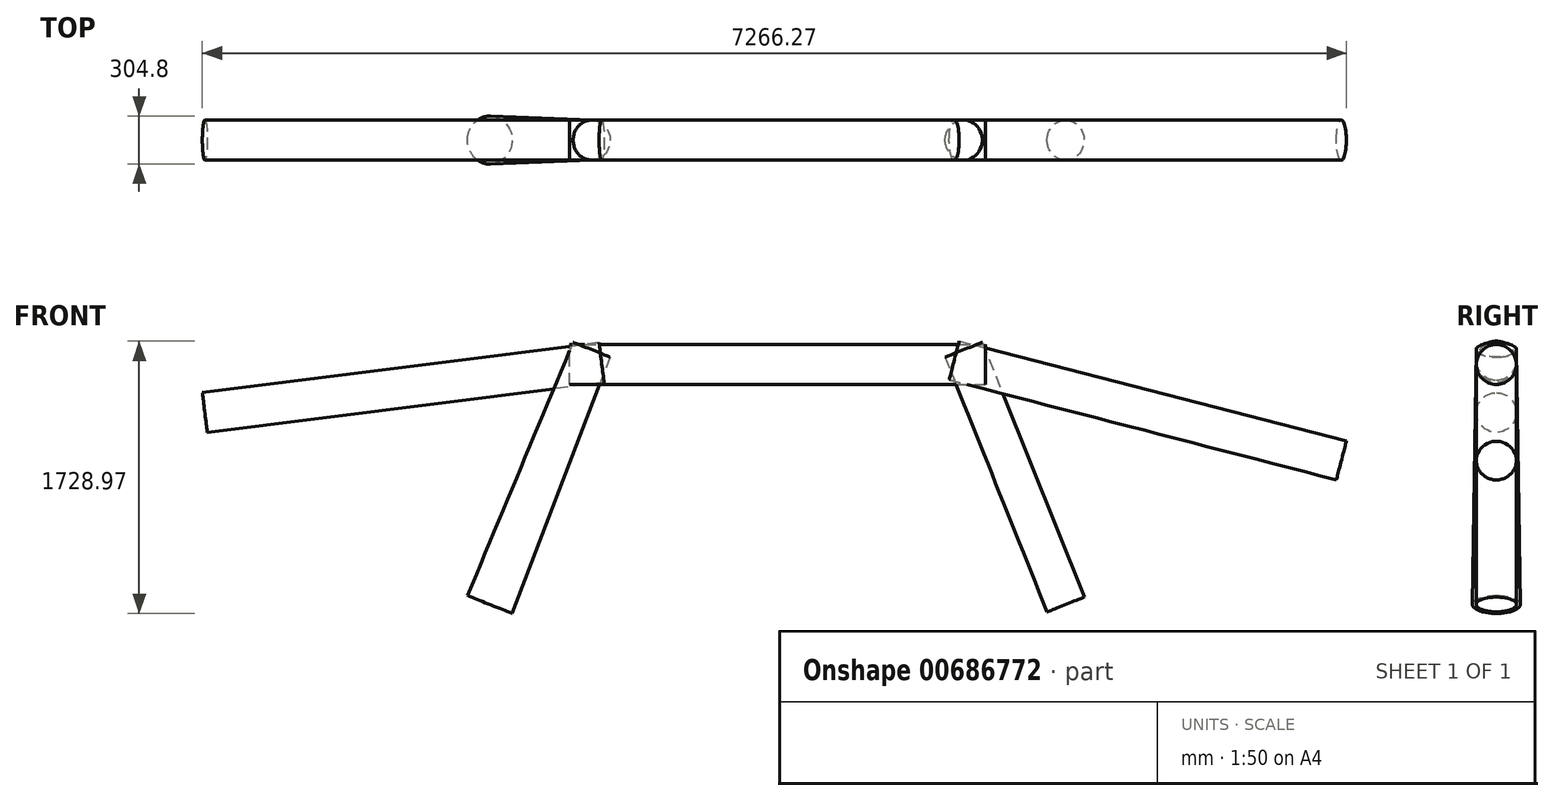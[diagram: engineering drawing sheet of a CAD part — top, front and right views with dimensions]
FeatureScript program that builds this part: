
annotation { "Feature Type Name" : "Feature", "Feature Type Description" : "" }
export const myFeature = defineFeature(function(context is Context, id is Id, definition is map)
    precondition{}
    {
        {
            var Q0;
            Q0=qCreatedBy(makeId("Front.planeOp"),FACE);
            var sketch = newSketch(context, id + "F0", { "sketchPlane" : qUnion([Q0])});
            skLineSegment(sketch, "E0", {"start": v(-1320.8, 0) * mm, "end": v(-1219.2, 0) * mm, "construction": true});
            skLineSegment(sketch, "E1", {"start": v(-1219.2, 0) * mm, "end": v(1219.2, 0) * mm, "construction": true});
            skLineSegment(sketch, "E2", {"start": v(1219.2, 0) * mm, "end": v(1320.8, 0) * mm, "construction": true});
            skLineSegment(sketch, "E3", {"start": v(-1181.47, 94.33) * mm, "end": v(-1219.2, 0) * mm, "construction": true});
            skLineSegment(sketch, "E4", {"start": v(-1219.2, 0) * mm, "end": v(-1828.8, -1524) * mm, "construction": true});
            skLineSegment(sketch, "E5", {"start": v(1181.47, 94.33) * mm, "end": v(1219.2, 0) * mm, "construction": true});
            skLineSegment(sketch, "E6", {"start": v(1219.2, 0) * mm, "end": v(1828.8, -1524) * mm, "construction": true});
            skLineSegment(sketch, "E7", {"start": v(1120.83, 25.4) * mm, "end": v(1219.2, 0) * mm, "construction": true});
            skLineSegment(sketch, "E8", {"start": v(1219.2, 0) * mm, "end": v(3580.17, -609.6) * mm, "construction": true});
            skLineSegment(sketch, "E9", {"start": v(-1118.4, 12.7) * mm, "end": v(-1219.2, 0) * mm, "construction": true});
            skLineSegment(sketch, "E10", {"start": v(-1219.2, 0) * mm, "end": v(-3638.47, -304.8) * mm, "construction": true});
            skSolve(sketch);
        }
        {
            var Q0;
            Q0=sQuery(id+"F0.wireOp",EDGE,"E10");
            var Q1;
            Q1=sQuery(id+"F0.wireOp",VERTEX,"E10.end");
            cPlane(context, id + "F1", {"entities" : qUnion([Q0, Q1]), "cplaneType" : CPlaneType.LINE_POINT, "offset" : 25.4 * mm, "width" : 152.4 * mm, "height" : 152.4 * mm});
        }
        {
            var Q0;
            Q0=sQuery(id+"F0.wireOp",VERTEX,"E9.start");
            var Q1;
            Q1=sQuery(id+"F0.wireOp",EDGE,"E9");
            cPlane(context, id + "F2", {"entities" : qUnion([Q0, Q1]), "cplaneType" : CPlaneType.LINE_POINT, "offset" : 25.4 * mm, "width" : 152.4 * mm, "height" : 152.4 * mm});
        }
        {
            var Q0;
            Q0=qCreatedBy(id+"F1.planeOp",FACE);
            var sketch = newSketch(context, id + "F3", { "sketchPlane" : qUnion([Q0])});
            skCircle(sketch, "E11", {"center": v(0, 152.4) * mm, "radius": 127 * mm});
            skSolve(sketch);
        }
        {
            var Q0;
            Q0=qCreatedBy(id+"F2.planeOp",FACE);
            var sketch = newSketch(context, id + "F4", { "sketchPlane" : qUnion([Q0])});
            skCircle(sketch, "E12", {"center": v(0, 152.4) * mm, "radius": 127 * mm});
            skSolve(sketch);
        }
        {
            var Q0;
            Q0=makeQuery(id+"F3.imprint","IMPRINT",FACE,{"disambiguationData":[TD([[makeQuery(id+"F3.imprint","IMPRINT",EDGE,{"derivedFrom":sQuery(id+"F3.wireOp",EDGE,"E11")}),1.0]])]});
            var Q1;
            Q1=makeQuery(id+"F4.imprint","IMPRINT",FACE,{"disambiguationData":[TD([[makeQuery(id+"F4.imprint","IMPRINT",EDGE,{"derivedFrom":sQuery(id+"F4.wireOp",EDGE,"E12")}),1.0]])]});
            loft(context, id + "F5", {"sheetProfilesArray" : [{ "sheetProfileEntities" : qUnion([Q0]) }, { "sheetProfileEntities" : qUnion([Q1]) }]});
        }
        {
            var Q0;
            Q0=sQuery(id+"F0.wireOp",EDGE,"E4");
            var Q1;
            Q1=sQuery(id+"F0.wireOp",VERTEX,"E4.end");
            cPlane(context, id + "F6", {"entities" : qUnion([Q0, Q1]), "cplaneType" : CPlaneType.LINE_POINT, "offset" : 25.4 * mm, "width" : 152.4 * mm, "height" : 152.4 * mm});
        }
        {
            var Q0;
            Q0=sQuery(id+"F0.wireOp",VERTEX,"E3.start");
            var Q1;
            Q1=sQuery(id+"F0.wireOp",EDGE,"E3");
            cPlane(context, id + "F7", {"entities" : qUnion([Q0, Q1]), "cplaneType" : CPlaneType.LINE_POINT, "offset" : 25.4 * mm, "width" : 152.4 * mm, "height" : 152.4 * mm});
        }
        {
            var Q0;
            Q0=qCreatedBy(id+"F6.planeOp",FACE);
            var sketch = newSketch(context, id + "F8", { "sketchPlane" : qUnion([Q0])});
            skCircle(sketch, "E13", {"center": v(-1132, 0) * mm, "radius": 152.4 * mm});
            skSolve(sketch);
        }
        {
            var Q0;
            Q0=qCreatedBy(id+"F7.planeOp",FACE);
            var sketch = newSketch(context, id + "F9", { "sketchPlane" : qUnion([Q0])});
            skCircle(sketch, "E14", {"center": v(-1132, 0) * mm, "radius": 127 * mm});
            skSolve(sketch);
        }
        {
            var Q0;
            Q0=makeQuery(id+"F8.imprint","IMPRINT",FACE,{"disambiguationData":[TD([[makeQuery(id+"F8.imprint","IMPRINT",EDGE,{"derivedFrom":sQuery(id+"F8.wireOp",EDGE,"E13")}),1.0]])]});
            var Q1;
            Q1=makeQuery(id+"F9.imprint","IMPRINT",FACE,{"disambiguationData":[TD([[makeQuery(id+"F9.imprint","IMPRINT",EDGE,{"derivedFrom":sQuery(id+"F9.wireOp",EDGE,"E14")}),1.0]])]});
            loft(context, id + "F10", {"sheetProfilesArray" : [{ "sheetProfileEntities" : qUnion([Q0]) }, { "sheetProfileEntities" : qUnion([Q1]) }]});
        }
        {
            var Q0;
            Q0=sQuery(id+"F0.wireOp",EDGE,"E0");
            var Q1;
            Q1=sQuery(id+"F0.wireOp",VERTEX,"E0.start");
            cPlane(context, id + "F11", {"entities" : qUnion([Q0, Q1]), "cplaneType" : CPlaneType.LINE_POINT, "offset" : 25.4 * mm, "width" : 152.4 * mm, "height" : 152.4 * mm});
        }
        {
            var Q0;
            Q0=sQuery(id+"F0.wireOp",EDGE,"E2");
            var Q1;
            Q1=sQuery(id+"F0.wireOp",VERTEX,"E2.end");
            cPlane(context, id + "F12", {"entities" : qUnion([Q0, Q1]), "cplaneType" : CPlaneType.LINE_POINT, "offset" : 25.4 * mm, "width" : 152.4 * mm, "height" : 152.4 * mm});
        }
        {
            var Q0;
            Q0=qCreatedBy(id+"F12.planeOp",FACE);
            var sketch = newSketch(context, id + "F13", { "sketchPlane" : qUnion([Q0])});
            skCircle(sketch, "E15", {"center": v(0, 0) * mm, "radius": 127 * mm});
            skSolve(sketch);
        }
        {
            var Q0;
            Q0=qCreatedBy(id+"F11.planeOp",FACE);
            var sketch = newSketch(context, id + "F14", { "sketchPlane" : qUnion([Q0])});
            skCircle(sketch, "E16", {"center": v(0, 0) * mm, "radius": 127 * mm});
            skSolve(sketch);
        }
        {
            var Q0;
            Q0=makeQuery(id+"F14.imprint","IMPRINT",FACE,{"disambiguationData":[TD([[makeQuery(id+"F14.imprint","IMPRINT",EDGE,{"derivedFrom":sQuery(id+"F14.wireOp",EDGE,"E16")}),1.0]])]});
            var Q1;
            Q1=makeQuery(id+"F13.imprint","IMPRINT",FACE,{"disambiguationData":[TD([[makeQuery(id+"F13.imprint","IMPRINT",EDGE,{"derivedFrom":sQuery(id+"F13.wireOp",EDGE,"E15")}),1.0]])]});
            loft(context, id + "F15", {"sheetProfilesArray" : [{ "sheetProfileEntities" : qUnion([Q0]) }, { "sheetProfileEntities" : qUnion([Q1]) }]});
        }
        {
            var Q0;
            Q0=sQuery(id+"F0.wireOp",VERTEX,"E8.end");
            var Q1;
            Q1=sQuery(id+"F0.wireOp",EDGE,"E8");
            cPlane(context, id + "F16", {"entities" : qUnion([Q0, Q1]), "cplaneType" : CPlaneType.LINE_POINT, "offset" : 25.4 * mm, "width" : 152.4 * mm, "height" : 152.4 * mm});
        }
        {
            var Q0;
            Q0=sQuery(id+"F0.wireOp",EDGE,"E7");
            var Q1;
            Q1=sQuery(id+"F0.wireOp",VERTEX,"E7.start");
            cPlane(context, id + "F17", {"entities" : qUnion([Q0, Q1]), "cplaneType" : CPlaneType.LINE_POINT, "offset" : 25.4 * mm, "width" : 152.4 * mm, "height" : 152.4 * mm});
        }
        {
            var Q0;
            Q0=qCreatedBy(id+"F16.planeOp",FACE);
            var sketch = newSketch(context, id + "F18", { "sketchPlane" : qUnion([Q0])});
            skCircle(sketch, "E17", {"center": v(0, 304.8) * mm, "radius": 127 * mm});
            skSolve(sketch);
        }
        {
            var Q0;
            Q0=qCreatedBy(id+"F17.planeOp",FACE);
            var sketch = newSketch(context, id + "F19", { "sketchPlane" : qUnion([Q0])});
            skCircle(sketch, "E18", {"center": v(0, 304.8) * mm, "radius": 127 * mm});
            skSolve(sketch);
        }
        {
            var Q0;
            Q0=makeQuery(id+"F18.imprint","IMPRINT",FACE,{"disambiguationData":[TD([[makeQuery(id+"F18.imprint","IMPRINT",EDGE,{"derivedFrom":sQuery(id+"F18.wireOp",EDGE,"E17")}),1.0]])]});
            var Q1;
            Q1=makeQuery(id+"F19.imprint","IMPRINT",FACE,{"disambiguationData":[TD([[makeQuery(id+"F19.imprint","IMPRINT",EDGE,{"derivedFrom":sQuery(id+"F19.wireOp",EDGE,"E18")}),1.0]])]});
            loft(context, id + "F20", {"sheetProfilesArray" : [{ "sheetProfileEntities" : qUnion([Q0]) }, { "sheetProfileEntities" : qUnion([Q1]) }]});
        }
        {
            var Q0;
            Q0=sQuery(id+"F0.wireOp",EDGE,"E6");
            var Q1;
            Q1=sQuery(id+"F0.wireOp",VERTEX,"E6.end");
            cPlane(context, id + "F21", {"entities" : qUnion([Q0, Q1]), "cplaneType" : CPlaneType.LINE_POINT, "offset" : 25.4 * mm, "width" : 152.4 * mm, "height" : 152.4 * mm});
        }
        {
            var Q0;
            Q0=sQuery(id+"F0.wireOp",EDGE,"E5");
            var Q1;
            Q1=sQuery(id+"F0.wireOp",VERTEX,"E5.start");
            cPlane(context, id + "F22", {"entities" : qUnion([Q0, Q1]), "cplaneType" : CPlaneType.LINE_POINT, "offset" : 25.4 * mm, "width" : 152.4 * mm, "height" : 152.4 * mm});
        }
        {
            var Q0;
            Q0=qCreatedBy(id+"F22.planeOp",FACE);
            var sketch = newSketch(context, id + "F23", { "sketchPlane" : qUnion([Q0])});
            skCircle(sketch, "E19", {"center": v(1132, 0) * mm, "radius": 127 * mm});
            skSolve(sketch);
        }
        {
            var Q0;
            Q0=qCreatedBy(id+"F21.planeOp",FACE);
            var sketch = newSketch(context, id + "F24", { "sketchPlane" : qUnion([Q0])});
            skCircle(sketch, "E20", {"center": v(1132, 0) * mm, "radius": 127 * mm});
            skSolve(sketch);
        }
        {
            var Q0;
            Q0=makeQuery(id+"F24.imprint","IMPRINT",FACE,{"disambiguationData":[TD([[makeQuery(id+"F24.imprint","IMPRINT",EDGE,{"derivedFrom":sQuery(id+"F24.wireOp",EDGE,"E20")}),1.0]])]});
            var Q1;
            Q1=makeQuery(id+"F23.imprint","IMPRINT",FACE,{"disambiguationData":[TD([[makeQuery(id+"F23.imprint","IMPRINT",EDGE,{"derivedFrom":sQuery(id+"F23.wireOp",EDGE,"E19")}),1.0]])]});
            loft(context, id + "F25", {"sheetProfilesArray" : [{ "sheetProfileEntities" : qUnion([Q0]) }, { "sheetProfileEntities" : qUnion([Q1]) }]});
        }
    });
